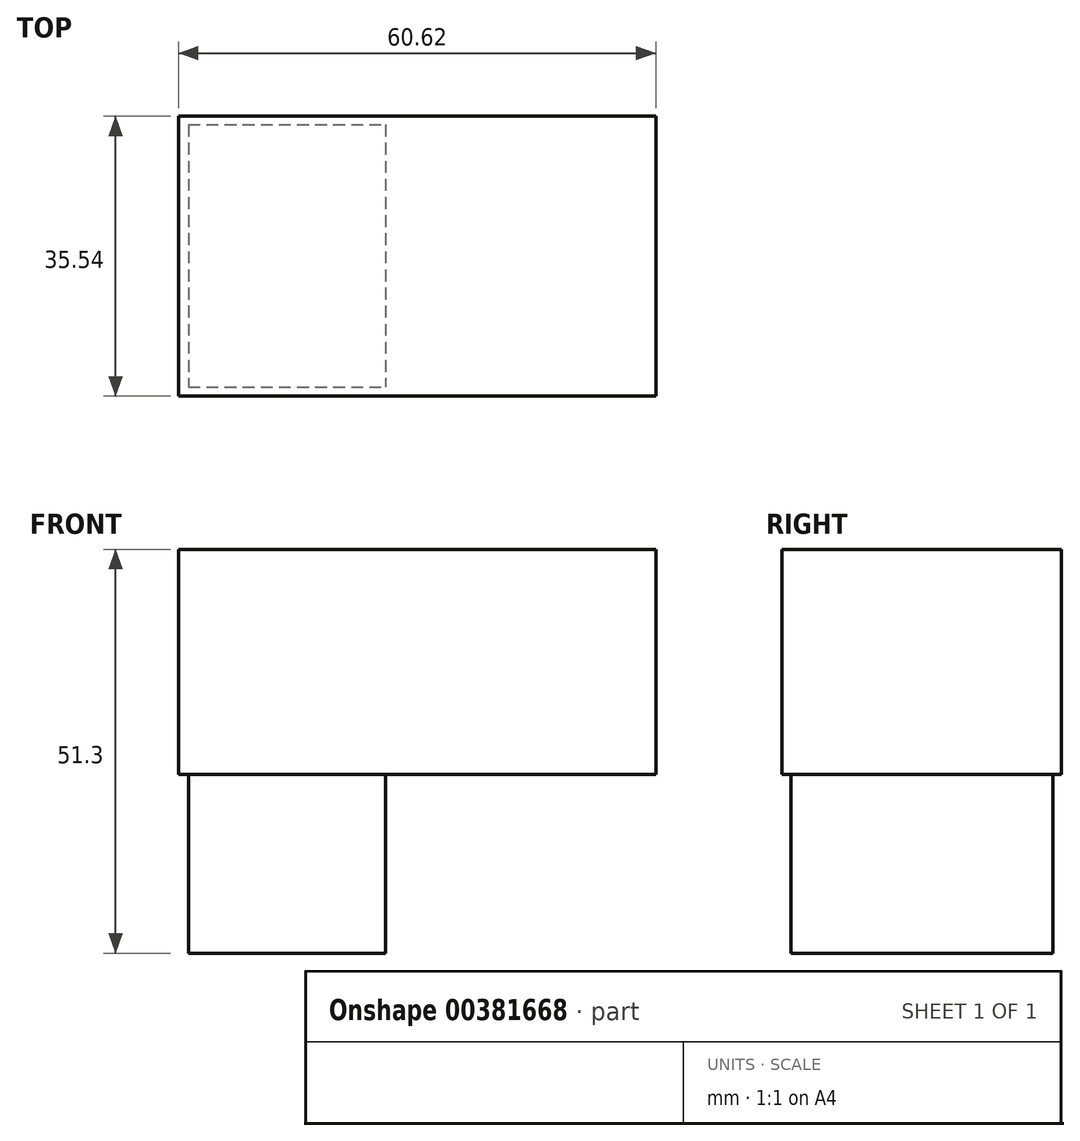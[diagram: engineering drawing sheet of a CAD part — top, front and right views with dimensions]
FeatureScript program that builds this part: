
annotation { "Feature Type Name" : "Feature", "Feature Type Description" : "" }
export const myFeature = defineFeature(function(context is Context, id is Id, definition is map)
    precondition{}
    {
        {
            var Q0;
            Q0=qCreatedBy(makeId("Top.planeOp"),FACE);
            var sketch = newSketch(context, id + "F0", { "sketchPlane" : qUnion([Q0])});
            skLineSegment(sketch, "E0.bottom", {"start": v(-30.58, -17.14) * mm, "end": v(30.04, -17.14) * mm});
            skLineSegment(sketch, "E0.top", {"start": v(-30.58, 18.4) * mm, "end": v(30.04, 18.4) * mm});
            skLineSegment(sketch, "E0.left", {"start": v(-30.58, -17.14) * mm, "end": v(-30.58, 18.4) * mm});
            skLineSegment(sketch, "E0.right", {"start": v(30.04, -17.14) * mm, "end": v(30.04, 18.4) * mm});
            skSolve(sketch);
        }
        {
            var Q0;
            Q0 = qSketchRegion(id + "F0", true);
            extrude(context, id + "F1", {"entities" : qUnion([Q0]), "depth" : 28.6 * mm});
        }
        {
            var Q0;
            Q0=qCreatedBy(makeId("Top.planeOp"),FACE);
            var sketch = newSketch(context, id + "F2", { "sketchPlane" : qUnion([Q0])});
            skLineSegment(sketch, "E1.bottom", {"start": v(-29.33, 17.33) * mm, "end": v(-4.3, 17.33) * mm});
            skLineSegment(sketch, "E1.top", {"start": v(-29.33, -15.97) * mm, "end": v(-4.3, -15.97) * mm});
            skLineSegment(sketch, "E1.left", {"start": v(-29.33, 17.33) * mm, "end": v(-29.33, -15.97) * mm});
            skLineSegment(sketch, "E1.right", {"start": v(-4.3, 17.33) * mm, "end": v(-4.3, -15.97) * mm});
            skSolve(sketch);
        }
        {
            var Q0;
            Q0 = qSketchRegion(id + "F2", true);
            extrude(context, id + "F3", {"entities" : qUnion([Q0]), "operationType" : NewBodyOperationType.ADD, "oppositeDirection" : true, "depth" : 22.7 * mm});
        }
    });
